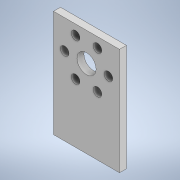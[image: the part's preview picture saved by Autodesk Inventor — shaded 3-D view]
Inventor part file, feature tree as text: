
AUTODESK INVENTOR PART (.ipt)
format: ipt  version: 2021 (Build 250183000, 183)  size: 147,456 bytes
history: native  units: in
note: dims shown in document units (in); Inventor stores cm internally (conversion verified against a paired STEP export)
features: sketch x3, extrude x2, hole x1
ambient origin geometry x8: Origin, YZ Plane, XZ Plane, XY Plane, X Axis, Y Axis, Z Axis, Center Point
bodies: Solid1 (feature_tree)
feature tree (6):
  extrude  "Extrusion1"  Depth=0.95in
  hole  "Hole1"  [1 undecoded]
  extrude  "Extrusion4"  Depth=0.95in
  sketch  "Sketch1"  dims[d0=1.54in d1=0.95in]
  sketch  "Sketch3"  dims[d2=0.1in d3=0.0in d7=0.076in]
  sketch  "Sketch5"  dims[d8=0.076in d9=0.0667in d10=0.172in d11=0.375in d12=0.25in d13=0.5635in d14=0.2275in d15=0.8108in d29=2.3622in d30=0.475in d31=0.275in d32=0.63in d33=0.125in d34=360.0deg d35=0.95in d36=1.124in d37=0.0in d38=0.0in d16=0.75in d17=0.8108in d18=0.0625in d19=0.75in d20=0.375in d26=0.5in d27=0.0344in d28=0.5in]
note: 1 required parameter value undecoded (feature->parameter linkage not recoverable at this tier; creation-order binding heuristic only, values carry confidence <= 0.55)
